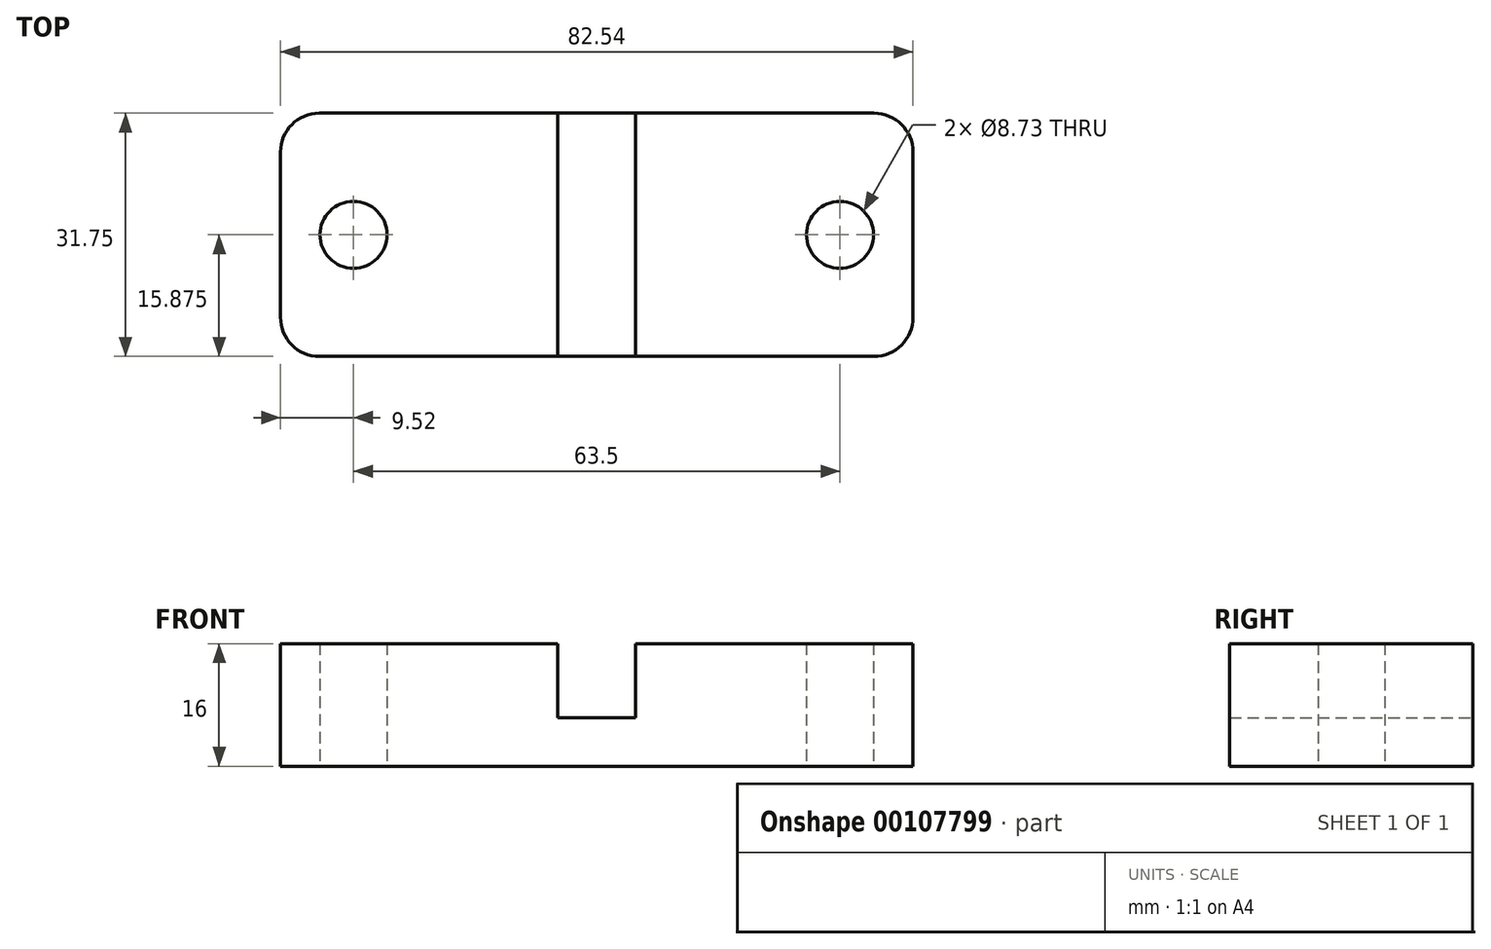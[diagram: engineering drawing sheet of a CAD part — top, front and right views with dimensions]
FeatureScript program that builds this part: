
annotation { "Feature Type Name" : "Feature", "Feature Type Description" : "" }
export const myFeature = defineFeature(function(context is Context, id is Id, definition is map)
    precondition{}
    {
        {
            var Q0;
            Q0=qCreatedBy(makeId("Front.planeOp"),FACE);
            var sketch = newSketch(context, id + "F0", { "sketchPlane" : qUnion([Q0])});
            skLineSegment(sketch, "E0.bottom", {"start": v(0, 0) * mm, "end": v(-5.08, 0) * mm});
            skLineSegment(sketch, "E0.top", {"start": v(0, -6.35) * mm, "end": v(-41.28, -6.35) * mm});
            skLineSegment(sketch, "E0.left", {"start": v(0, 0) * mm, "end": v(0, -6.35) * mm});
            skLineSegment(sketch, "E0.right", {"start": v(-41.28, 0) * mm, "end": v(-41.28, -6.35) * mm});
            skLineSegment(sketch, "E1.top", {"start": v(-5.08, 9.65) * mm, "end": v(-41.28, 9.65) * mm});
            skLineSegment(sketch, "E1.left", {"start": v(-5.08, 0) * mm, "end": v(-5.08, 9.65) * mm});
            skLineSegment(sketch, "E1.right", {"start": v(-41.28, 0) * mm, "end": v(-41.28, 9.65) * mm});
            skSolve(sketch);
        }
        {
            var Q0;
            Q0=makeQuery(id+"F0.imprint","IMPRINT",FACE,{"disambiguationData":[TD([[makeQuery(id+"F0.imprint","IMPRINT",EDGE,{"derivedFrom":sQuery(id+"F0.wireOp",EDGE,"E0.bottom")}),1.0]])]});
            extrude(context, id + "F1", {"entities" : qUnion([Q0]), "depth" : 31.75 * mm});
        }
        {
            var Q0;
            Q0=makeQuery(id+"F1.opExtrude","CAP_EDGE",EDGE,{"disambiguationData":[OSD([sQuery(id+"F0.wireOp",EDGE,"E0.right"),sQuery(id+"F0.wireOp",EDGE,"E1.right")])],"isStart":false});
            var Q1;
            Q1=makeQuery(id+"F1.opExtrude","CAP_EDGE",EDGE,{"disambiguationData":[OSD([sQuery(id+"F0.wireOp",EDGE,"E0.right"),sQuery(id+"F0.wireOp",EDGE,"E1.right")])],"isStart":true});
            fillet(context, id + "F2", {"entities" : qUnion([Q0, Q1]), "radius" : 5.08 * mm, "tangentPropagation" : true, "allowEdgeOverflow" : false});
        }
        {
            var Q0;
            Q0=makeQuery(id+"F1.opExtrude","SWEPT_FACE",FACE,{"disambiguationData":[OSD([sQuery(id+"F0.wireOp",EDGE,"E0.top")])]});
            var sketch = newSketch(context, id + "F3", { "sketchPlane" : qUnion([Q0])});
            skCircle(sketch, "E2", {"center": v(-31.75, 15.87) * mm, "radius": 2.7 * mm});
            skSolve(sketch);
        }
        {
            var Q0;
            Q0=sQuery(id+"F3.wireOp",VERTEX,"E2.center");
            var Q1;
            Q1=makeQuery(id+"F1.opExtrude","SWEPT_BODY",BODY,{"disambiguationData":[OSD([sQuery(id+"F0.wireOp",EDGE,"E0.bottom"),sQuery(id+"F0.wireOp",EDGE,"E0.top"),sQuery(id+"F0.wireOp",EDGE,"E0.left"),sQuery(id+"F0.wireOp",EDGE,"E0.right"),sQuery(id+"F0.wireOp",EDGE,"E1.top"),sQuery(id+"F0.wireOp",EDGE,"E1.left"),sQuery(id+"F0.wireOp",EDGE,"E1.right")])]});
            hole(context, id + "F4", {"style" : HoleStyle.SIMPLE, "endStyle" : HoleEndStyle.THROUGH, "holeDiameter" : 8.73 * mm, "locations" : qUnion([Q0]), "scope" : qUnion([Q1]), "isTappedThrough" : true});
        }
        {
            var Q0;
            Q0=makeQuery(id+"F1.opExtrude","SWEPT_BODY",BODY,{"disambiguationData":[OSD([sQuery(id+"F0.wireOp",EDGE,"E0.bottom"),sQuery(id+"F0.wireOp",EDGE,"E0.top"),sQuery(id+"F0.wireOp",EDGE,"E0.left"),sQuery(id+"F0.wireOp",EDGE,"E0.right"),sQuery(id+"F0.wireOp",EDGE,"E1.top"),sQuery(id+"F0.wireOp",EDGE,"E1.left"),sQuery(id+"F0.wireOp",EDGE,"E1.right")])]});
            var Q1;
            Q1=qCreatedBy(makeId("Right.planeOp"),FACE);
            mirror(context, id + "F5", {"operationType" : NewBodyOperationType.ADD, "entities" : qUnion([Q0]), "mirrorPlane" : qUnion([Q1])});
        }
    });
